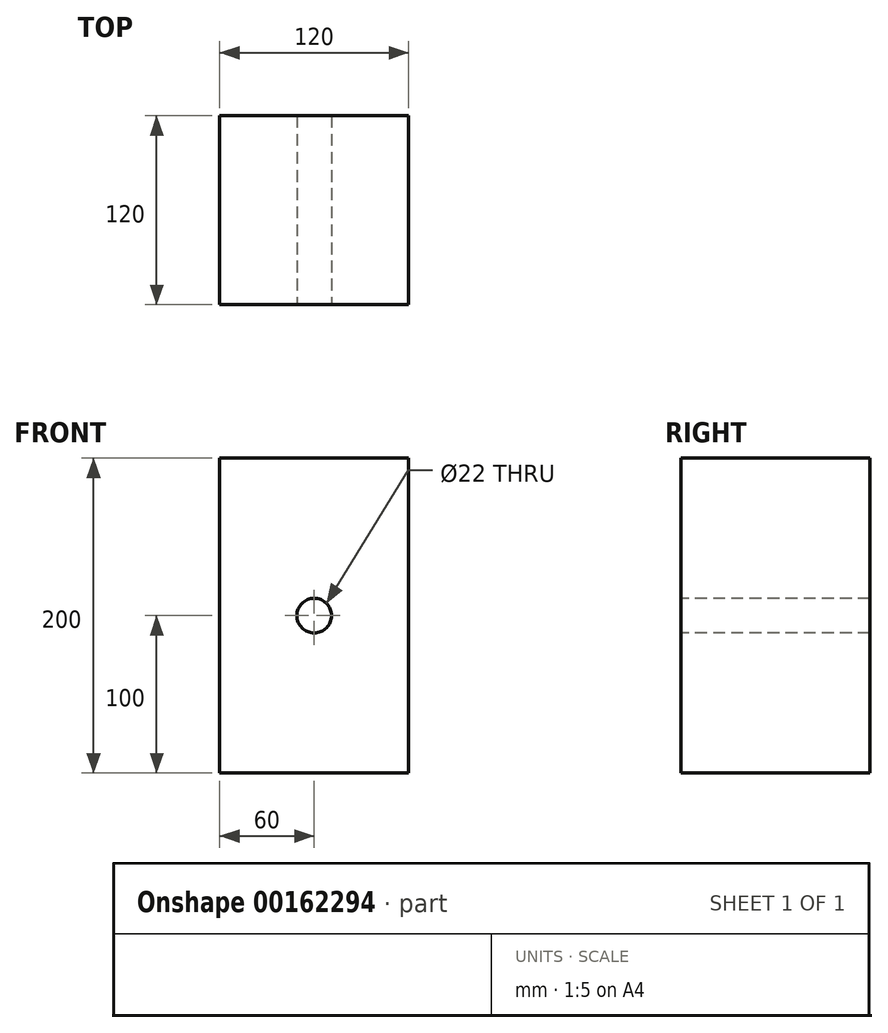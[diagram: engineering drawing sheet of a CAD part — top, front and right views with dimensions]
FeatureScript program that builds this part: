
annotation { "Feature Type Name" : "Feature", "Feature Type Description" : "" }
export const myFeature = defineFeature(function(context is Context, id is Id, definition is map)
    precondition{}
    {
        {
            var Q0;
            Q0=qCreatedBy(makeId("Front.planeOp"),FACE);
            var sketch = newSketch(context, id + "F0", { "sketchPlane" : qUnion([Q0])});
            skLineSegment(sketch, "E0.bottom", {"start": v(-60, 100) * mm, "end": v(60, 100) * mm});
            skLineSegment(sketch, "E0.top", {"start": v(-60, -100) * mm, "end": v(60, -100) * mm});
            skLineSegment(sketch, "E0.left", {"start": v(-60, 100) * mm, "end": v(-60, -100) * mm});
            skLineSegment(sketch, "E0.right", {"start": v(60, 100) * mm, "end": v(60, -100) * mm});
            skPoint(sketch, "E0.middle", {"position": v(0, 0) * mm});
            skSolve(sketch);
        }
        {
            var Q0;
            Q0=makeQuery(id+"F0.imprint","IMPRINT",FACE,{"disambiguationData":[TD([[makeQuery(id+"F0.imprint","IMPRINT",EDGE,{"derivedFrom":sQuery(id+"F0.wireOp",EDGE,"E0.bottom")}),-1.0]])]});
            extrude(context, id + "F1", {"entities" : qUnion([Q0]), "depth" : 120 * mm});
        }
        {
            var Q0;
            Q0=makeQuery(id+"F1.opExtrude","CAP_FACE",FACE,{"disambiguationData":[OSD([sQuery(id+"F0.wireOp",EDGE,"E0.bottom"),sQuery(id+"F0.wireOp",EDGE,"E0.top"),sQuery(id+"F0.wireOp",EDGE,"E0.left"),sQuery(id+"F0.wireOp",EDGE,"E0.right")])],"isStart":false});
            var sketch = newSketch(context, id + "F2", { "sketchPlane" : qUnion([Q0])});
            skCircle(sketch, "E1", {"center": v(0, 0) * mm, "radius": 10.06 * mm});
            skSolve(sketch);
        }
        {
            var Q0;
            Q0=sQuery(id+"F2.wireOp",VERTEX,"NzXTTxk8-TJvl-U40K-xiCM-UWxMStuBWoF0.center");
            var Q1;
            Q1=sQuery(id+"F2.wireOp",VERTEX,"E1.center");
            var Q2;
            Q2=makeQuery(id+"F1.opExtrude","SWEPT_BODY",BODY,{"disambiguationData":[OSD([sQuery(id+"F0.wireOp",EDGE,"E0.bottom"),sQuery(id+"F0.wireOp",EDGE,"E0.top"),sQuery(id+"F0.wireOp",EDGE,"E0.left"),sQuery(id+"F0.wireOp",EDGE,"E0.right")])]});
            hole(context, id + "F3", {"style" : HoleStyle.SIMPLE, "endStyle" : HoleEndStyle.THROUGH, "holeDiameter" : 22 * mm, "startFromSketch" : true, "locations" : qUnion([Q0, Q1]), "scope" : qUnion([Q2]), "isTappedThrough" : true});
        }
    });
